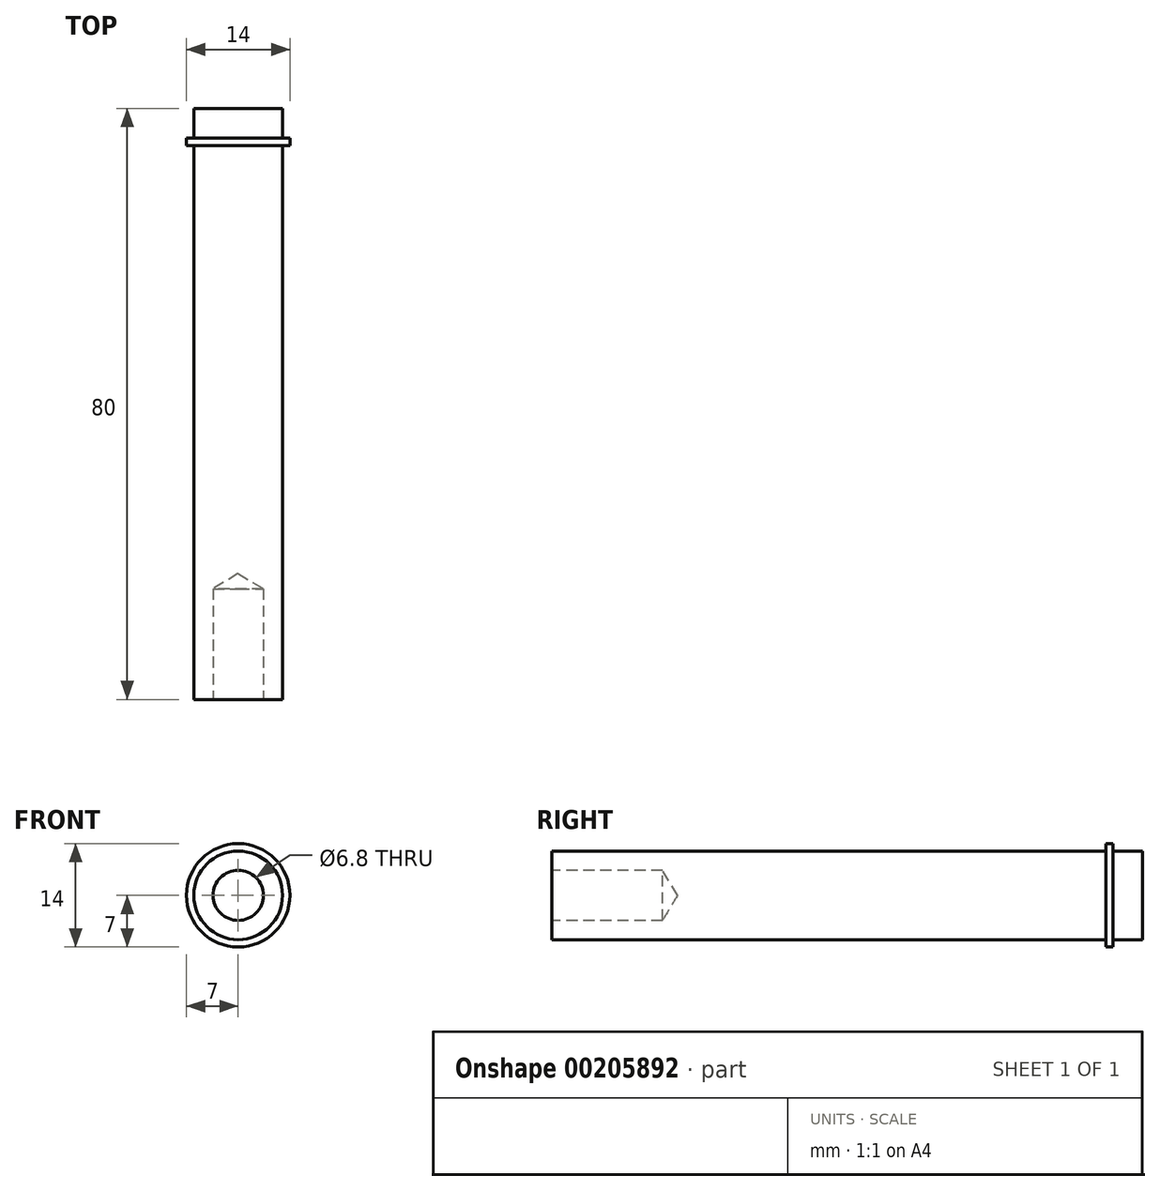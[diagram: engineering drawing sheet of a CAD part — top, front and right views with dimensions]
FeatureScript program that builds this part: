
annotation { "Feature Type Name" : "Feature", "Feature Type Description" : "" }
export const myFeature = defineFeature(function(context is Context, id is Id, definition is map)
    precondition{}
    {
        {
            var Q0;
            Q0=qCreatedBy(makeId("Front.planeOp"),FACE);
            var sketch = newSketch(context, id + "F0", { "sketchPlane" : qUnion([Q0])});
            skCircle(sketch, "E0", {"center": v(0, 0) * mm, "radius": 6 * mm});
            skSolve(sketch);
        }
        {
            var Q0;
            Q0=makeQuery(id+"F0.imprint","IMPRINT",FACE,{"disambiguationData":[TD([[makeQuery(id+"F0.imprint","IMPRINT",EDGE,{"derivedFrom":sQuery(id+"F0.wireOp",EDGE,"E0")}),1.0]])]});
            extrude(context, id + "F1", {"entities" : qUnion([Q0]), "depth" : 75 * mm});
        }
        {
            var Q0;
            Q0=makeQuery(id+"F1.opExtrude","CAP_FACE",FACE,{"disambiguationData":[OSD([sQuery(id+"F0.wireOp",EDGE,"E0")])],"isStart":true});
            var sketch = newSketch(context, id + "F2", { "sketchPlane" : qUnion([Q0])});
            skCircle(sketch, "E1", {"center": v(0, 0) * mm, "radius": 7 * mm});
            skSolve(sketch);
        }
        {
            var Q0;
            Q0=makeQuery(id+"F2.imprint","IMPRINT",FACE,{"disambiguationData":[TD([[makeQuery(id+"F2.imprint","IMPRINT",EDGE,{"derivedFrom":sQuery(id+"F2.wireOp",EDGE,"E1")}),1.0]])]});
            var Q1;
            Q1=makeQuery(id+"F2.imprint","IMPRINT",FACE,{"disambiguationData":[TD([[makeQuery(id+"F2.imprint","IMPRINT",EDGE,{"derivedFrom":makeQuery(id+"F1.opExtrude","CAP_EDGE",EDGE,{"disambiguationData":[OSD([sQuery(id+"F0.wireOp",EDGE,"E0")])],"isStart":true})}),-1.0]])]});
            extrude(context, id + "F3", {"entities" : qUnion([Q0, Q1]), "operationType" : NewBodyOperationType.ADD, "depth" : 1 * mm});
        }
        {
            var Q0;
            Q0=makeQuery(id+"F3.opExtrude","CAP_FACE",FACE,{"disambiguationData":[OSD([sQuery(id+"F2.wireOp",EDGE,"E1")])],"isStart":false});
            var sketch = newSketch(context, id + "F4", { "sketchPlane" : qUnion([Q0])});
            skCircle(sketch, "E2", {"center": v(0, 0) * mm, "radius": 6 * mm});
            skSolve(sketch);
        }
        {
            var Q0;
            Q0 = qSketchRegion(id + "F4", true);
            extrude(context, id + "F5", {"entities" : qUnion([Q0]), "operationType" : NewBodyOperationType.ADD, "depth" : 4 * mm});
        }
        {
            var Q0;
            Q0=makeQuery(id+"F1.opExtrude","CAP_FACE",FACE,{"disambiguationData":[OSD([sQuery(id+"F0.wireOp",EDGE,"E0")])],"isStart":false});
            var sketch = newSketch(context, id + "F6", { "sketchPlane" : qUnion([Q0])});
            skPoint(sketch, "E3", {"position": v(0, 0) * mm});
            skSolve(sketch);
        }
        {
            var Q0;
            Q0=sQuery(id+"F6.wireOp",VERTEX,"E3");
            var Q1;
            Q1=makeQuery(id+"F1.opExtrude","SWEPT_BODY",BODY,{"disambiguationData":[OSD([sQuery(id+"F0.wireOp",EDGE,"E0")])]});
            hole(context, id + "F7", {"style" : HoleStyle.SIMPLE, "endStyle" : HoleEndStyle.BLIND, "standardTappedOrClearance" : lookupTablePath({ "standard" : "ISO", "engagement" : "75%", "pitch" : "1.25 mm", "size" : "M8", "type" : "Tapped" }), "standardBlindInLast" : lookupTablePath({ "standard" : "ISO", "engagement" : "75%", "pitch" : "1.25 mm", "size" : "M8", "type" : "Tapped" }), "holeDiameter" : 6.8 * mm, "holeDepth" : 15 * mm, "locations" : qUnion([Q0]), "scope" : qUnion([Q1]), "majorDiameter" : 8 * mm});
        }
    });
